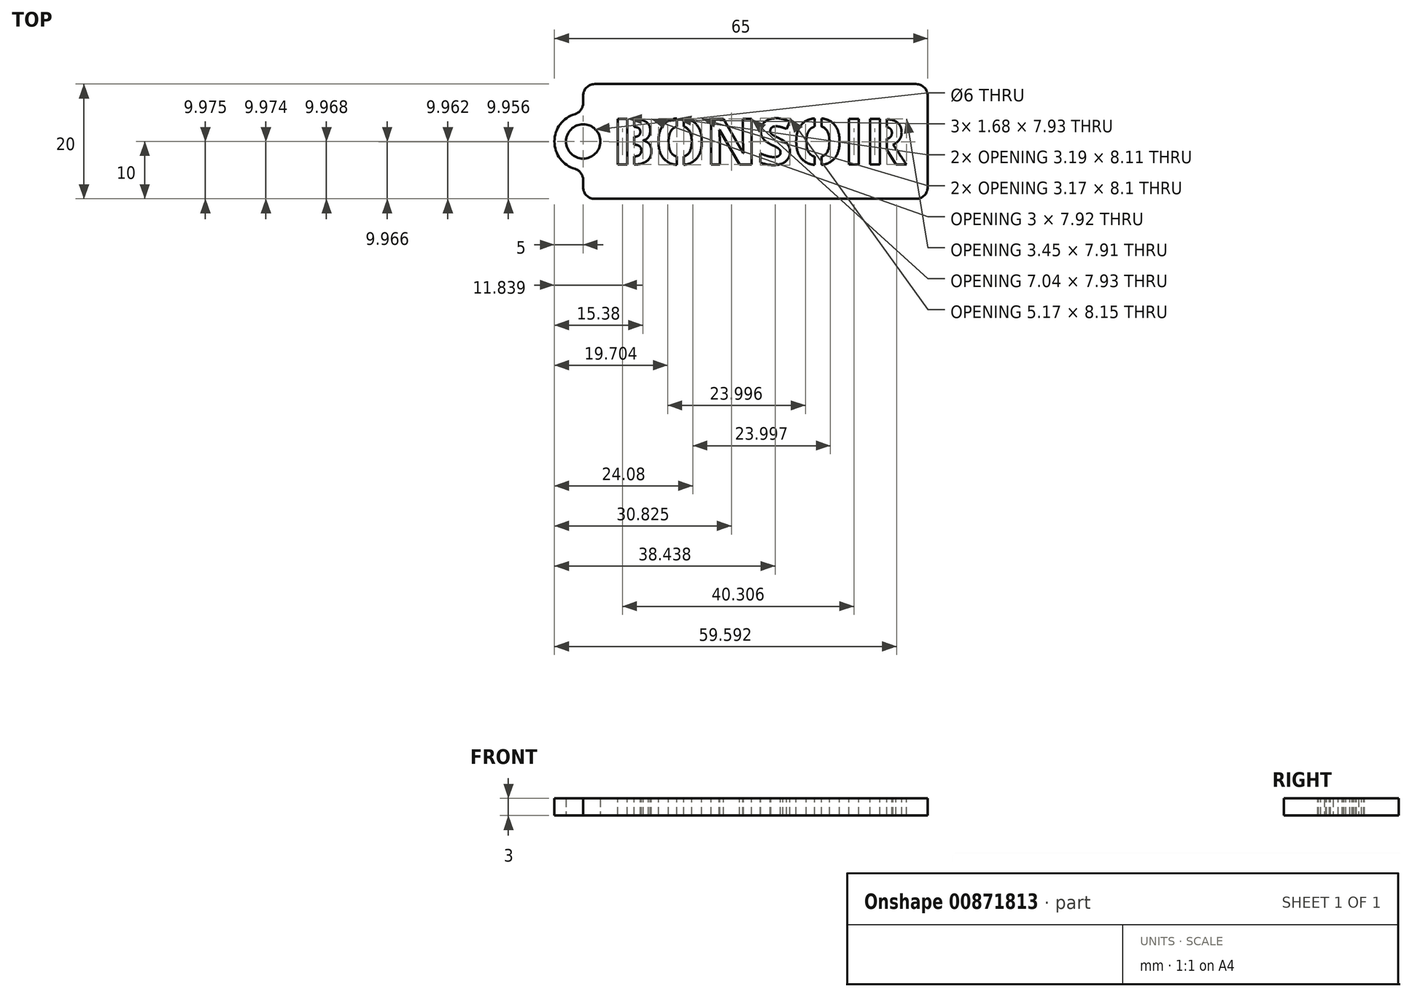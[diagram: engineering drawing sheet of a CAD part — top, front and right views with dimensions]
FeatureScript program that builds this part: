
annotation { "Feature Type Name" : "Feature", "Feature Type Description" : "" }
export const myFeature = defineFeature(function(context is Context, id is Id, definition is map)
    precondition{}
    {
        {
            var Q0;
            Q0=qCreatedBy(makeId("Top.planeOp"),FACE);
            var sketch = newSketch(context, id + "F0", { "sketchPlane" : qUnion([Q0])});
            skLineSegment(sketch, "E0.bottom", {"start": v(30, -10) * mm, "end": v(-30, -10) * mm});
            skLineSegment(sketch, "E0.top", {"start": v(30, 10) * mm, "end": v(-30, 10) * mm});
            skLineSegment(sketch, "E0.left", {"start": v(30, -10) * mm, "end": v(30, 10) * mm});
            skLineSegment(sketch, "E0.right", {"start": v(-30, -10) * mm, "end": v(-30, -5) * mm});
            skPoint(sketch, "E0.middle", {"position": v(0, 0) * mm});
            skArc(sketch, "E1", {"start": v(-30, 5) * mm, "mid": v(-35, 0) * mm, "end": v(-30, -5) * mm});
            skCircle(sketch, "E2", {"center": v(-30, 0) * mm, "radius": 3 * mm});
            skLineSegment(sketch, "E3.trimOffspring", {"start": v(-30, 5) * mm, "end": v(-30, 10) * mm});
            skSolve(sketch);
        }
        {
            var Q0;
            Q0 = qSketchRegion(id + "F0", true);
            extrude(context, id + "F1", {"entities" : qUnion([Q0]), "depth" : 3 * mm, "offsetDistance" : 25 * mm});
        }
        {
            var Q0;
            Q0=makeQuery(id+"F1.opExtrude","CAP_FACE",FACE,{"disambiguationData":[OSD([sQuery(id+"F0.wireOp",EDGE,"E0.bottom"),sQuery(id+"F0.wireOp",EDGE,"E0.top"),sQuery(id+"F0.wireOp",EDGE,"E0.left"),sQuery(id+"F0.wireOp",EDGE,"E0.right"),sQuery(id+"F0.wireOp",EDGE,"E1"),sQuery(id+"F0.wireOp",EDGE,"E2"),sQuery(id+"F0.wireOp",EDGE,"E3.trimOffspring")])],"isStart":false});
            var sketch = newSketch(context, id + "F2", { "sketchPlane" : qUnion([Q0])});
            skText(sketch, "E4", { "text": "BONSOIR", "fontName": "OpenSans-Bold.ttf"});
            skLineSegment(sketch, "E5", {"start": v(34.27, 0) * mm, "end": v(25.76, 0) * mm, "construction": true});
            const initialGuessF2  = {"E4": [-0.025, -0.004, 1, 0, 0.008]};
            skSetInitialGuess(sketch, initialGuessF2);
            skSolve(sketch);
        }
        {
            var Q0;
            Q0 = qSketchRegion(id + "F2", true);
            extrude(context, id + "F3", {"entities" : qUnion([Q0]), "operationType" : NewBodyOperationType.REMOVE, "endBound" : BoundingType.THROUGH_ALL, "oppositeDirection" : true, "depth" : 25 * mm, "offsetDistance" : 25 * mm});
        }
        {
            var Q0;
            {var subQ0=sQuery(id+"F0.wireOp",EDGE,"E3.trimOffspring");var subQ1=sQuery(id+"F0.wireOp",EDGE,"E2");var subQ2=sQuery(id+"F0.wireOp",EDGE,"E0.bottom");var subQ3=sQuery(id+"F0.wireOp",EDGE,"E1");var subQ4=sQuery(id+"F0.wireOp",EDGE,"E0.right");var subQ5=sQuery(id+"F0.wireOp",EDGE,"E0.top");var subQ6=sQuery(id+"F0.wireOp",EDGE,"E0.left");Q0=makeQuery(id+"F3.boolean.opBoolean","SPLIT",FACE,{"disambiguationData":[TD([makeQuery(id+"F1.opExtrude","SWEPT_FACE",FACE,{"disambiguationData":[OSD([subQ2])]})])],"derivedFrom":makeQuery(id+"F1.opExtrude","CAP_FACE",FACE,{"disambiguationData":[OSD([subQ2,subQ5,subQ6,subQ4,subQ3,subQ1,subQ0])],"isStart":false})});}
            var sketch = newSketch(context, id + "F4", { "sketchPlane" : qUnion([Q0])});
            skLineSegment(sketch, "E6.bottom", {"start": v(-22.32, 6.81) * mm, "end": v(-21.12, 6.81) * mm});
            skLineSegment(sketch, "E6.top", {"start": v(-22.32, -5.74) * mm, "end": v(-21.12, -5.74) * mm});
            skLineSegment(sketch, "E6.left", {"start": v(-22.32, 6.81) * mm, "end": v(-22.32, -5.74) * mm});
            skLineSegment(sketch, "E6.right", {"start": v(-21.12, 6.81) * mm, "end": v(-21.12, -5.74) * mm});
            skLineSegment(sketch, "E7.bottom", {"start": v(-13.7, 5.72) * mm, "end": v(-12.5, 5.72) * mm});
            skLineSegment(sketch, "E7.top", {"start": v(-13.7, -6.21) * mm, "end": v(-12.5, -6.21) * mm});
            skLineSegment(sketch, "E7.left", {"start": v(-13.7, 5.72) * mm, "end": v(-13.7, -6.21) * mm});
            skLineSegment(sketch, "E7.right", {"start": v(-12.5, 5.72) * mm, "end": v(-12.5, -6.21) * mm});
            skLineSegment(sketch, "E8", {"start": v(-13.1, 6.99) * mm, "end": v(-13.1, -8.56) * mm, "construction": true});
            skLineSegment(sketch, "E9.bottom", {"start": v(10.3, 6.22) * mm, "end": v(11.5, 6.22) * mm});
            skLineSegment(sketch, "E9.top", {"start": v(10.3, -5.7) * mm, "end": v(11.5, -5.7) * mm});
            skLineSegment(sketch, "E9.left", {"start": v(10.3, 6.22) * mm, "end": v(10.3, -5.7) * mm});
            skLineSegment(sketch, "E9.right", {"start": v(11.5, 6.22) * mm, "end": v(11.5, -5.7) * mm});
            skLineSegment(sketch, "E10", {"start": v(10.9, 7.49) * mm, "end": v(10.9, -8.05) * mm, "construction": true});
            skLineSegment(sketch, "E11.bottom", {"start": v(21.66, -1.63) * mm, "end": v(22.86, -1.63) * mm});
            skLineSegment(sketch, "E11.top", {"start": v(21.66, 5.97) * mm, "end": v(22.86, 5.97) * mm});
            skLineSegment(sketch, "E11.left", {"start": v(21.66, -1.63) * mm, "end": v(21.66, 5.97) * mm});
            skLineSegment(sketch, "E11.right", {"start": v(22.86, -1.63) * mm, "end": v(22.86, 5.97) * mm});
            skSolve(sketch);
        }
        {
            var Q0;
            Q0 = qSketchRegion(id + "F4", true);
            extrude(context, id + "F5", {"entities" : qUnion([Q0]), "operationType" : NewBodyOperationType.ADD, "oppositeDirection" : true, "depth" : 3 * mm, "offsetDistance" : 25 * mm});
        }
        {
            var Q0;
            Q0=makeQuery(id+"F1.opExtrude","SWEPT_EDGE",EDGE,{"disambiguationData":[OSD([sQuery(id+"F0.wireOp",EDGE,"E0.bottom"),sQuery(id+"F0.wireOp",EDGE,"E0.right")])]});
            var Q1;
            Q1=makeQuery(id+"F1.opExtrude","SWEPT_EDGE",EDGE,{"disambiguationData":[OSD([sQuery(id+"F0.wireOp",EDGE,"E0.top"),sQuery(id+"F0.wireOp",EDGE,"E3.trimOffspring")])]});
            var Q2;
            Q2=makeQuery(id+"F1.opExtrude","SWEPT_EDGE",EDGE,{"disambiguationData":[OSD([sQuery(id+"F0.wireOp",EDGE,"E1"),sQuery(id+"F0.wireOp",EDGE,"E3.trimOffspring")])]});
            var Q3;
            Q3=makeQuery(id+"F1.opExtrude","SWEPT_EDGE",EDGE,{"disambiguationData":[OSD([sQuery(id+"F0.wireOp",EDGE,"E0.right"),sQuery(id+"F0.wireOp",EDGE,"E1")])]});
            var Q4;
            Q4=makeQuery(id+"F1.opExtrude","SWEPT_EDGE",EDGE,{"disambiguationData":[OSD([sQuery(id+"F0.wireOp",EDGE,"E0.bottom"),sQuery(id+"F0.wireOp",EDGE,"E0.left")])]});
            var Q5;
            Q5=makeQuery(id+"F1.opExtrude","SWEPT_EDGE",EDGE,{"disambiguationData":[OSD([sQuery(id+"F0.wireOp",EDGE,"E0.top"),sQuery(id+"F0.wireOp",EDGE,"E0.left")])]});
            fillet(context, id + "F6", {"entities" : qUnion([Q0, Q1, Q2, Q3, Q4, Q5]), "radius" : 2 * mm, "tangentPropagation" : true, "allowEdgeOverflow" : false});
        }
    });
